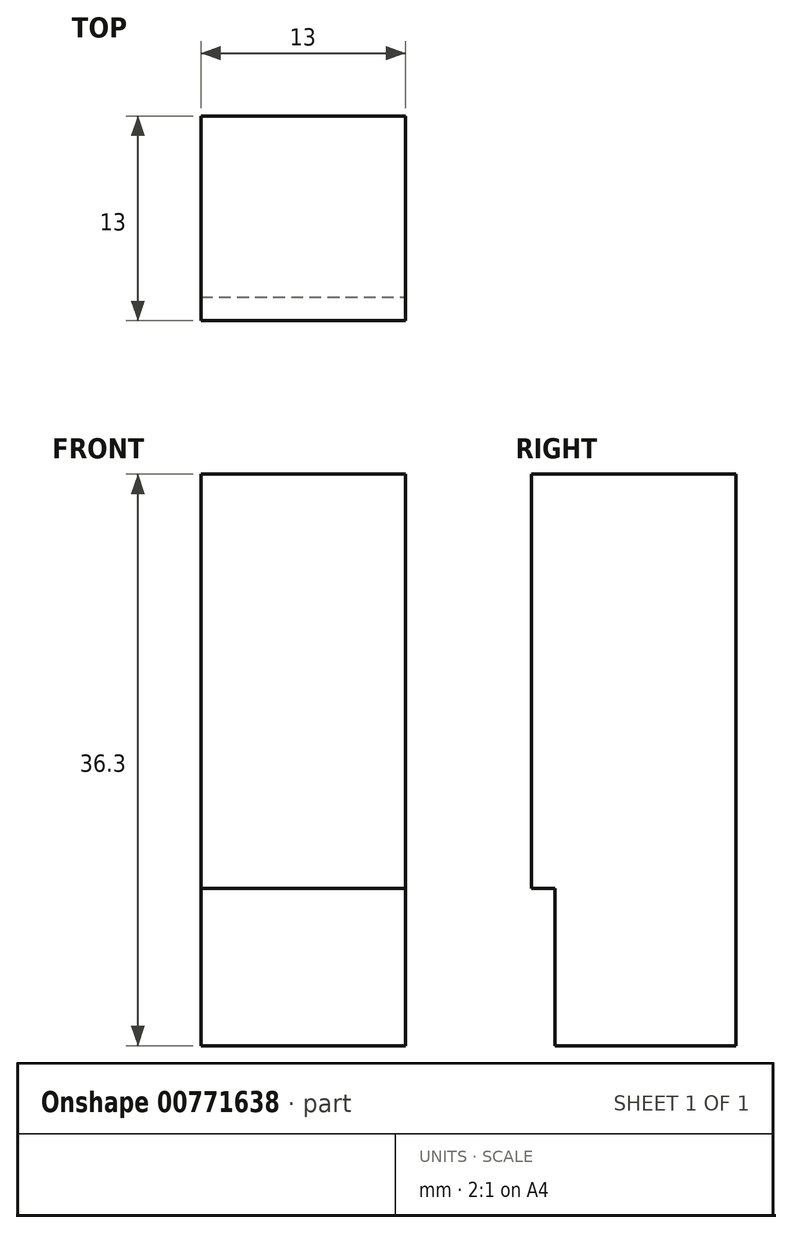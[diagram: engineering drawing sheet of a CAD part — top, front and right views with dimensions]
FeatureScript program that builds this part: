
annotation { "Feature Type Name" : "Feature", "Feature Type Description" : "" }
export const myFeature = defineFeature(function(context is Context, id is Id, definition is map)
    precondition{}
    {
        {
            var Q0;
            Q0=qCreatedBy(makeId("Top.planeOp"),FACE);
            var sketch = newSketch(context, id + "F0", { "sketchPlane" : qUnion([Q0])});
            skLineSegment(sketch, "E0.bottom", {"start": v(0.79, 6.5) * mm, "end": v(13.79, 6.5) * mm});
            skLineSegment(sketch, "E0.top", {"start": v(0.79, -6.5) * mm, "end": v(13.79, -6.5) * mm});
            skLineSegment(sketch, "E0.left", {"start": v(0.79, 6.5) * mm, "end": v(0.79, -6.5) * mm});
            skLineSegment(sketch, "E0.right", {"start": v(13.79, 6.5) * mm, "end": v(13.79, -6.5) * mm});
            skSolve(sketch);
        }
        {
            var Q0;
            Q0 = qSketchRegion(id + "F0", true);
            extrude(context, id + "F1", {"entities" : qUnion([Q0]), "depth" : 36.3 * mm, "offsetDistance" : 25 * mm});
        }
        {
            var Q0;
            Q0=makeQuery(id+"F1.opExtrude","CAP_FACE",FACE,{"disambiguationData":[OSD([sQuery(id+"F0.wireOp",EDGE,"E0.bottom"),sQuery(id+"F0.wireOp",EDGE,"E0.top"),sQuery(id+"F0.wireOp",EDGE,"E0.left"),sQuery(id+"F0.wireOp",EDGE,"E0.right")])],"isStart":true});
            var sketch = newSketch(context, id + "F2", { "sketchPlane" : qUnion([Q0])});
            skLineSegment(sketch, "E1.top", {"start": v(0.79, 5) * mm, "end": v(13.79, 5) * mm});
            skLineSegment(sketch, "E2.bottom", {"start": v(0.79, 6.5) * mm, "end": v(13.79, 6.5) * mm});
            skLineSegment(sketch, "E2.left", {"start": v(0.79, 6.5) * mm, "end": v(0.79, 5) * mm});
            skLineSegment(sketch, "E2.right", {"start": v(13.79, 6.5) * mm, "end": v(13.79, 5) * mm});
            skSolve(sketch);
        }
        {
            var Q0;
            Q0 = qSketchRegion(id + "F2", true);
            extrude(context, id + "F3", {"entities" : qUnion([Q0]), "operationType" : NewBodyOperationType.REMOVE, "oppositeDirection" : true, "depth" : 10 * mm, "offsetDistance" : 25 * mm});
        }
    });
